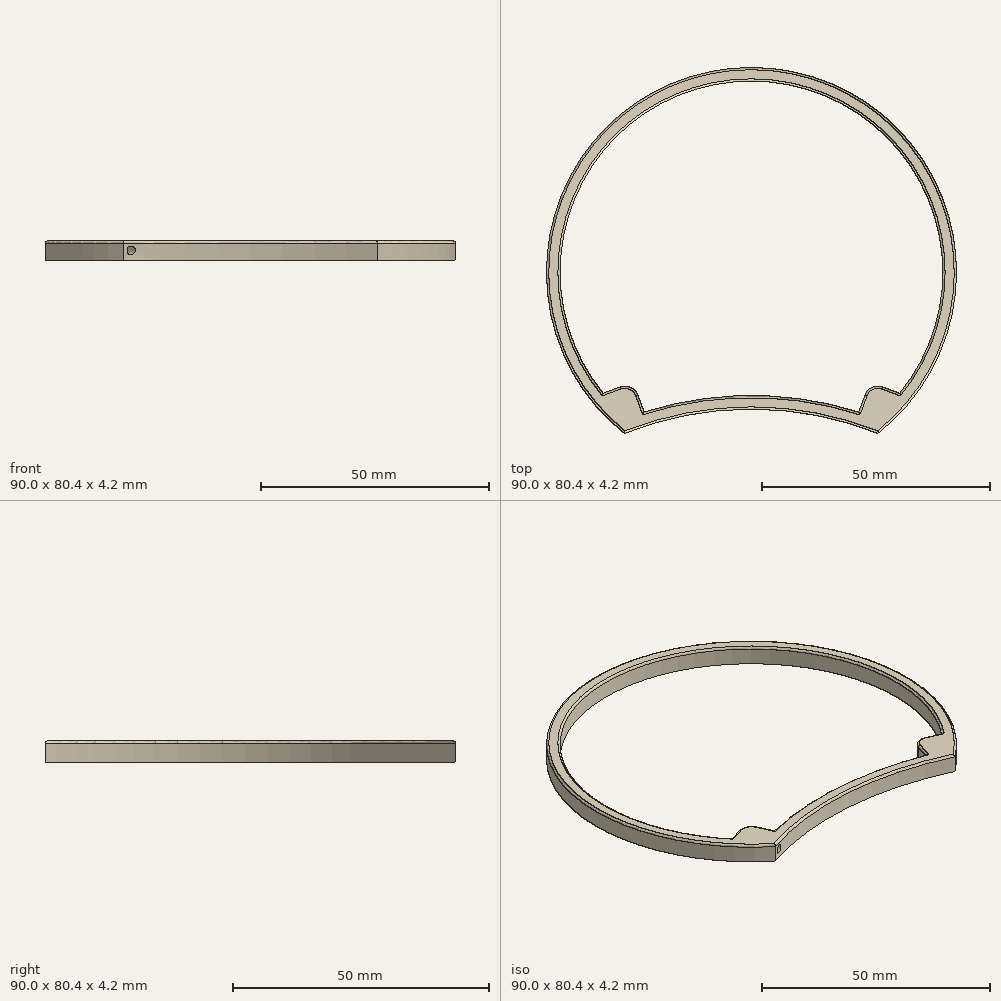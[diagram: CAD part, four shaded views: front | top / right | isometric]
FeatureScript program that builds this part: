
annotation { "Feature Type Name" : "Feature", "Feature Type Description" : "" }
export const myFeature = defineFeature(function(context is Context, id is Id, definition is map)
    precondition{}
    {
        {
            var Q0;
            Q0=qCreatedBy(makeId("Front.planeOp"),FACE);
            var sketch = newSketch(context, id + "F0", { "sketchPlane" : qUnion([Q0]), "disableImprinting" : false});
            skLineSegment(sketch, "E0.bottom", {"start": v(42, 4.2) * mm, "end": v(45, 4.2) * mm});
            skLineSegment(sketch, "E0.top", {"start": v(42, 0) * mm, "end": v(45, 0) * mm});
            skLineSegment(sketch, "E0.left", {"start": v(42, 4.2) * mm, "end": v(42, 0) * mm});
            skLineSegment(sketch, "E0.right", {"start": v(45, 4.2) * mm, "end": v(45, 0) * mm});
            skLineSegment(sketch, "E1", {"start": v(0, 23.86) * mm, "end": v(0, -32.38) * mm, "construction": true});
            skSolve(sketch);
        }
        {
            var Q0;
            Q0=makeQuery(id+"F0.imprint","IMPRINT",FACE,{"disambiguationData":[TD([[makeQuery(id+"F0.imprint","IMPRINT",EDGE,{"derivedFrom":sQuery(id+"F0.wireOp",EDGE,"E0.bottom")}),-1.0]])]});
            var Q1;
            Q1=sQuery(id+"F0.wireOp",EDGE,"E1");
            revolve(context, id + "F1", {"surfaceOperationType" : NewSurfaceOperationType.NEW, "entities" : qUnion([Q0]), "axis" : qUnion([Q1]), "revolveType" : RevolveType.FULL});
        }
        {
            var Q0;
            Q0=qCreatedBy(makeId("Top.planeOp"),FACE);
            var sketch = newSketch(context, id + "F2", { "sketchPlane" : qUnion([Q0])});
            skCircle(sketch, "E2", {"center": v(0, -105) * mm, "radius": 78 * mm});
            skCircle(sketch, "E3.0", {"center": v(0, 0) * mm, "radius": 45 * mm});
            skCircle(sketch, "E4.0", {"center": v(0, 0) * mm, "radius": 42 * mm});
            skCircle(sketch, "E5.0", {"center": v(0, -105) * mm, "radius": 75 * mm});
            skSolve(sketch);
        }
        {
            var Q0;
            {var subQ0=sQuery(id+"F2.wireOp",EDGE,"E4.0");var subQ1=sQuery(id+"F2.wireOp",EDGE,"E2");var subQ2=makeQuery(id+"F2.imprint","INTERSECT",VERTEX,{"disambiguationData":[OD(0.0)],"derivedFrom":[subQ1,subQ0]});Q0=makeQuery(id+"F2.imprint","IMPRINT",FACE,{"disambiguationData":[TD([[makeQuery(id+"F2.imprint","IMPRINT",EDGE,{"disambiguationData":[TD([[subQ2,-1.0]])],"derivedFrom":subQ1}),1.0]])]});}
            var Q1;
            Q1=makeQuery(id+"F1.opRevolve","SWEPT_FACE",FACE,{"disambiguationData":[OSD([sQuery(id+"F0.wireOp",EDGE,"E0.bottom")])]});
            extrude(context, id + "F3", {"entities" : qUnion([Q0]), "operationType" : NewBodyOperationType.ADD, "endBound" : BoundingType.UP_TO_SURFACE, "depth" : 25 * mm, "endBoundEntityFace" : qUnion([Q1]), "offsetDistance" : 25 * mm});
        }
        {
            var Q0;
            {var subQ0=sQuery(id+"F2.wireOp",EDGE,"E5.0");var subQ1=sQuery(id+"F2.wireOp",EDGE,"E4.0");var subQ2=makeQuery(id+"F2.imprint","INTERSECT",VERTEX,{"disambiguationData":[OD(0.0)],"derivedFrom":[subQ1,subQ0]});Q0=makeQuery(id+"F2.imprint","IMPRINT",FACE,{"disambiguationData":[TD([[makeQuery(id+"F2.imprint","IMPRINT",EDGE,{"disambiguationData":[TD([[subQ2,-1.0]])],"derivedFrom":subQ1}),1.0]])]});}
            var Q1;
            {var subQ0=sQuery(id+"F2.wireOp",EDGE,"E5.0");var subQ1=sQuery(id+"F2.wireOp",EDGE,"E3.0");var subQ2=makeQuery(id+"F2.imprint","INTERSECT",VERTEX,{"disambiguationData":[OD(0.0)],"derivedFrom":[subQ1,subQ0]});Q1=makeQuery(id+"F2.imprint","IMPRINT",FACE,{"disambiguationData":[TD([[makeQuery(id+"F2.imprint","IMPRINT",EDGE,{"disambiguationData":[TD([[subQ2,-1.0]])],"derivedFrom":subQ1}),1.0]])]});}
            extrude(context, id + "F4", {"entities" : qUnion([Q0, Q1]), "operationType" : NewBodyOperationType.REMOVE, "depth" : 25 * mm, "offsetDistance" : 25 * mm});
        }
        {
            var Q0;
            Q0=qCreatedBy(makeId("Top.planeOp"),FACE);
            var sketch = newSketch(context, id + "F5", { "sketchPlane" : qUnion([Q0]), "disableImprinting" : false});
            skArc(sketch, "E6.0", {"start": v(27.29, -31.93) * mm, "mid": v(0, 42) * mm, "end": v(-27.29, -31.93) * mm});
            skArc(sketch, "E6.1", {"start": v(27.29, -31.93) * mm, "mid": v(0, -27) * mm, "end": v(-27.29, -31.93) * mm});
            skLineSegment(sketch, "E7", {"start": v(-32.56, -26.53) * mm, "end": v(-26, -24.08) * mm});
            skLineSegment(sketch, "E8", {"start": v(-26, -24.08) * mm, "end": v(-23.55, -30.64) * mm});
            skLineSegment(sketch, "E9", {"start": v(-17.74, -28.37) * mm, "end": v(-42.66, -37.67) * mm, "construction": true});
            skLineSegment(sketch, "E10", {"start": v(0, 30.3) * mm, "end": v(0, -50.73) * mm, "construction": true});
            skLineSegment(sketch, "E11.MirrorCS", {"start": v(26, -24.08) * mm, "end": v(23.55, -30.64) * mm});
            skLineSegment(sketch, "E12.MirrorCS", {"start": v(32.56, -26.53) * mm, "end": v(26, -24.08) * mm});
            skSolve(sketch);
        }
        {
            var Q0;
            {var subQ0=sQuery(id+"F5.wireOp",EDGE,"E7");Q0=makeQuery(id+"F5.imprint","IMPRINT",FACE,{"disambiguationData":[TD([[makeQuery(id+"F5.imprint","IMPRINT",EDGE,{"derivedFrom":subQ0}),-1.0]])]});}
            var Q1;
            {var subQ4=sQuery(id+"F5.wireOp",EDGE,"E11.MirrorCS");Q1=makeQuery(id+"F5.imprint","IMPRINT",FACE,{"disambiguationData":[TD([[makeQuery(id+"F5.imprint","IMPRINT",EDGE,{"derivedFrom":subQ4}),1.0]])]});}
            var Q2;
            Q2=makeQuery(id+"F3.boolean.opBoolean","MERGE",FACE,{"derivedFrom":[makeQuery(id+"F1.opRevolve","SWEPT_FACE",FACE,{"disambiguationData":[OSD([sQuery(id+"F0.wireOp",EDGE,"E0.bottom")])]}),makeQuery(id+"F3.opExtrude","CAP_FACE",FACE,{"disambiguationData":[OSD([sQuery(id+"F2.wireOp",EDGE,"E2"),sQuery(id+"F2.wireOp",EDGE,"E4.0"),sQuery(id+"F2.wireOp",EDGE,"E5.0")])],"isStart":false})]});
            extrude(context, id + "F6", {"entities" : qUnion([Q0, Q1]), "operationType" : NewBodyOperationType.ADD, "endBound" : BoundingType.UP_TO_SURFACE, "depth" : 25 * mm, "endBoundEntityFace" : qUnion([Q2]), "offsetDistance" : 25 * mm});
        }
        {
            var Q0;
            Q0=makeQuery(id+"F6.opExtrude","SWEPT_EDGE",EDGE,{"disambiguationData":[OSD([sQuery(id+"F5.wireOp",EDGE,"E6.0"),sQuery(id+"F5.wireOp",EDGE,"E7")])]});
            var Q1;
            Q1=makeQuery(id+"F6.opExtrude","SWEPT_EDGE",EDGE,{"disambiguationData":[OSD([sQuery(id+"F5.wireOp",EDGE,"E7"),sQuery(id+"F5.wireOp",EDGE,"E8")])]});
            var Q2;
            Q2=makeQuery(id+"F6.opExtrude","SWEPT_EDGE",EDGE,{"disambiguationData":[OSD([sQuery(id+"F5.wireOp",EDGE,"E6.1"),sQuery(id+"F5.wireOp",EDGE,"E8")])]});
            var Q3;
            Q3=makeQuery(id+"F6.opExtrude","SWEPT_EDGE",EDGE,{"disambiguationData":[OSD([sQuery(id+"F5.wireOp",EDGE,"E11.MirrorCS"),sQuery(id+"F5.wireOp",EDGE,"E12.MirrorCS")])]});
            var Q4;
            Q4=makeQuery(id+"F6.opExtrude","SWEPT_EDGE",EDGE,{"disambiguationData":[OSD([sQuery(id+"F5.wireOp",EDGE,"E6.0"),sQuery(id+"F5.wireOp",EDGE,"E12.MirrorCS")])]});
            var Q5;
            Q5=makeQuery(id+"F6.opExtrude","SWEPT_EDGE",EDGE,{"disambiguationData":[OSD([sQuery(id+"F5.wireOp",EDGE,"E6.1"),sQuery(id+"F5.wireOp",EDGE,"E11.MirrorCS")])]});
            fillet(context, id + "F7", {"entities" : qUnion([Q0, Q1, Q2, Q3, Q4, Q5]), "tangentPropagation" : true, "radius" : 3 * mm, "defaultsChanged" : false, "vertexSettings" : [], "allowEdgeOverflow" : false});
        }
        {
            var Q0;
            Q0=makeQuery(id+"F6.opExtrude","SWEPT_FACE",FACE,{"disambiguationData":[OSD([sQuery(id+"F5.wireOp",EDGE,"E7")])]});
            var sketch = newSketch(context, id + "F8", { "sketchPlane" : qUnion([Q0]), "disableImprinting" : false});
            skLineSegment(sketch, "E13", {"start": v(36.68, 0) * mm, "end": v(36.68, 4.2) * mm, "construction": true});
            skCircle(sketch, "E14", {"center": v(36.68, 2.1) * mm, "radius": 0.95 * mm});
            skSolve(sketch);
        }
        {
            var Q0;
            Q0 = qSketchRegion(id + "F8", true);
            var Q1;
            Q1 = qConstructionFilter(qBodyType(qCreatedBy(id + "F8" ,EDGE), BodyType.WIRE), ConstructionObject.NO);
            extrude(context, id + "F9", {"entities" : qUnion([Q0]), "operationType" : NewBodyOperationType.REMOVE, "surfaceEntities" : qUnion([Q1]), "oppositeDirection" : true, "depth" : 25 * mm, "offsetDistance" : 25 * mm});
        }
        {
            var Q0;
            Q0=makeQuery(id+"F1.opRevolve","SWEPT_FACE",FACE,{"disambiguationData":[OSD([sQuery(id+"F0.wireOp",EDGE,"E0.bottom")])]});
            fillet(context, id + "F10", {"entities" : qUnion([Q0]), "tangentPropagation" : true, "radius" : 0.5 * mm, "defaultsChanged" : true, "vertexSettings" : [], "allowEdgeOverflow" : false});
        }
    });
